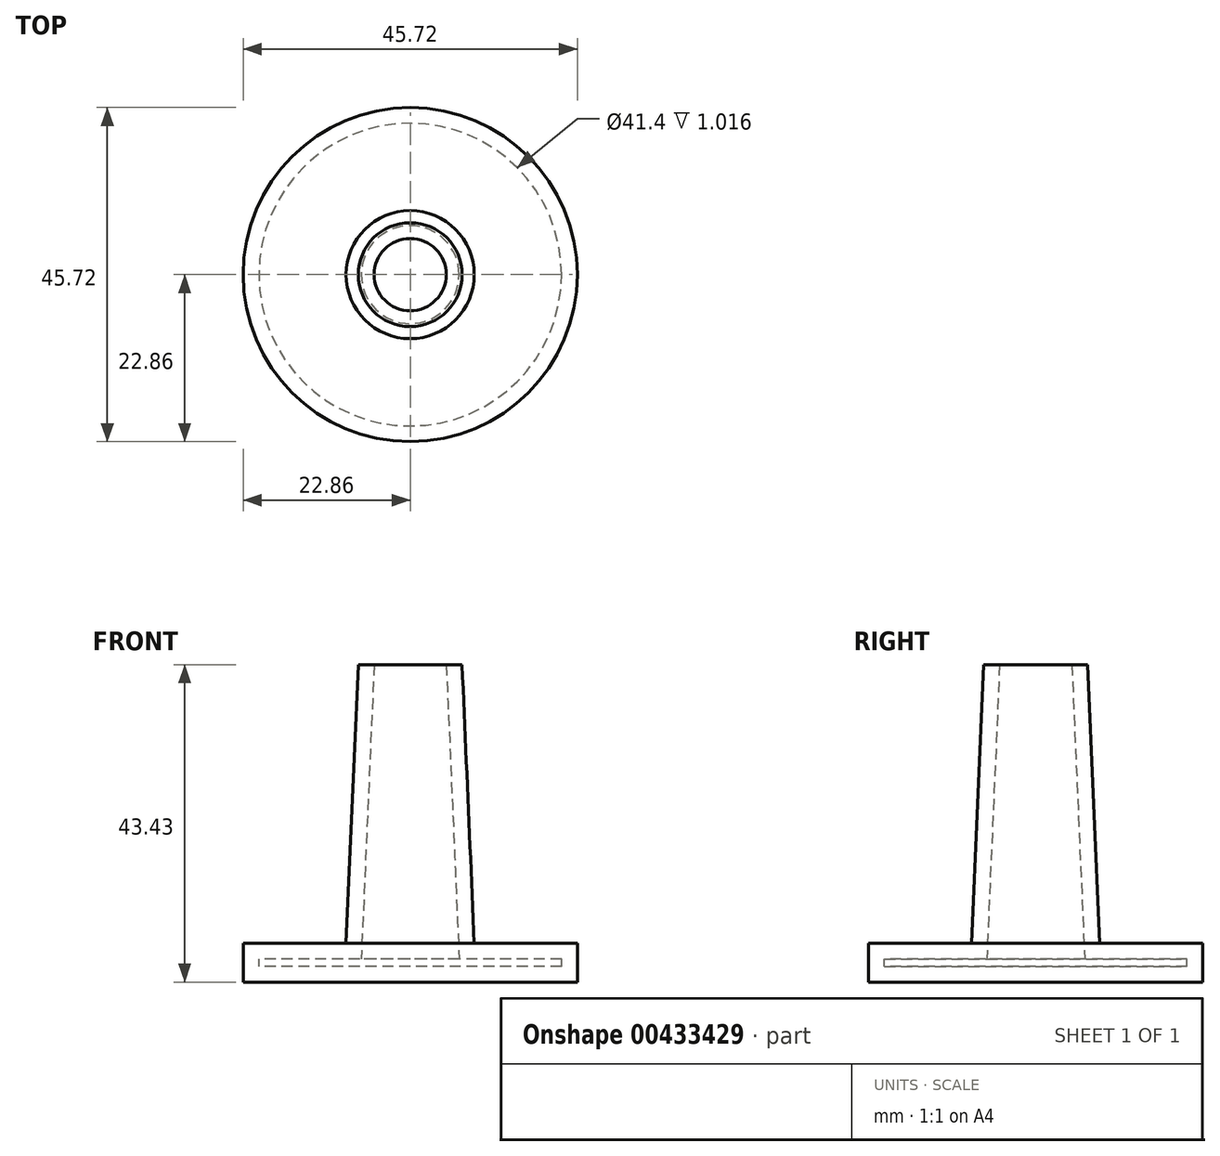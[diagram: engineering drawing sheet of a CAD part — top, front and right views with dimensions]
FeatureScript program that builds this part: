
annotation { "Feature Type Name" : "Feature", "Feature Type Description" : "" }
export const myFeature = defineFeature(function(context is Context, id is Id, definition is map)
    precondition{}
    {
        {
            var Q0;
            Q0=qCreatedBy(makeId("Top.planeOp"),FACE);
            var sketch = newSketch(context, id + "F0", { "sketchPlane" : qUnion([Q0])});
            skCircle(sketch, "E0", {"center": v(0, 0) * mm, "radius": 22.86 * mm});
            skSolve(sketch);
        }
        {
            var Q0;
            Q0 = qSketchRegion(id + "F0", true);
            extrude(context, id + "F1", {"entities" : qUnion([Q0]), "oppositeDirection" : true, "depth" : 5.33 * mm});
        }
        {
            var Q0;
            Q0=qCreatedBy(makeId("Top.planeOp"),FACE);
            var sketch = newSketch(context, id + "F2", { "sketchPlane" : qUnion([Q0])});
            skCircle(sketch, "E1", {"center": v(0, 0) * mm, "radius": 8.76 * mm});
            skSolve(sketch);
        }
        {
            var Q0;
            Q0 = qSketchRegion(id + "F2", true);
            extrude(context, id + "F3", {"entities" : qUnion([Q0]), "operationType" : NewBodyOperationType.ADD, "depth" : 38.1 * mm, "hasDraft" : true, "draftAngle" : 2.5 * degree, "draftPullDirection" : true});
        }
        {
            var Q0;
            Q0=makeQuery(id+"F3.opExtrude","CAP_FACE",FACE,{"disambiguationData":[OSD([sQuery(id+"F2.wireOp",EDGE,"E1")])],"isStart":false});
            var Q1;
            Q1=makeQuery(id+"F1.opExtrude","SWEPT_BODY",BODY,{"disambiguationData":[OSD([sQuery(id+"F0.wireOp",EDGE,"E0")])]});
            shell(context, id + "F4", {"entities" : qUnion([Q0]), "parts" : qUnion([Q1]), "thickness" : 2.16 * mm});
        }
    });
